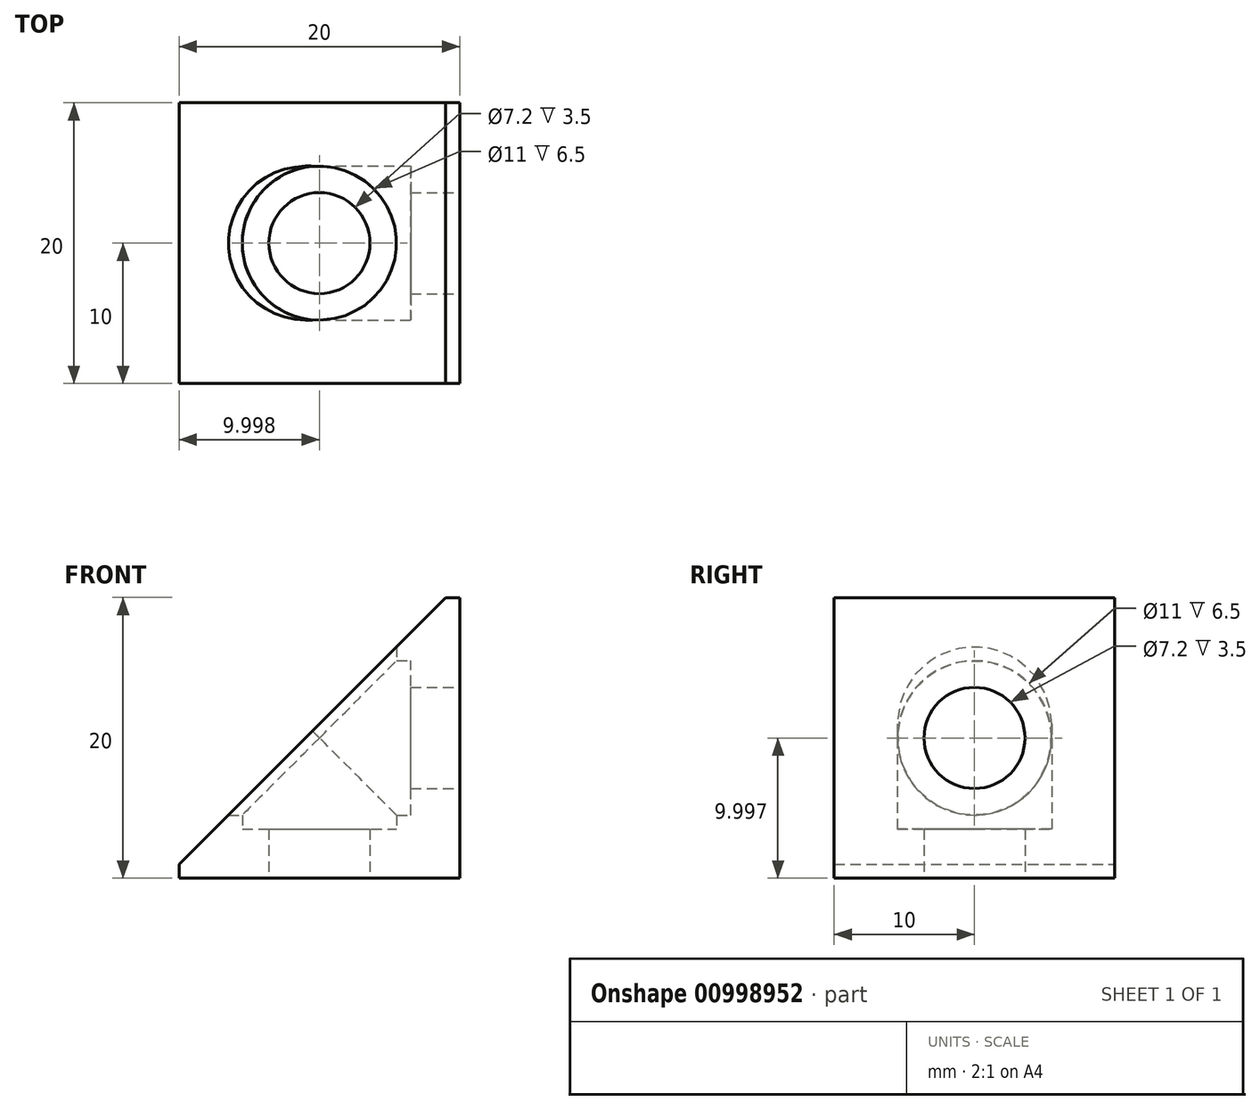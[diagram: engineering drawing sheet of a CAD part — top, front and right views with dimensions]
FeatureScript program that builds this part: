
annotation { "Feature Type Name" : "Feature", "Feature Type Description" : "" }
export const myFeature = defineFeature(function(context is Context, id is Id, definition is map)
    precondition{}
    {
        {
            var Q0;
            Q0=qCreatedBy(makeId("Front.planeOp"),FACE);
            var sketch = newSketch(context, id + "F0", { "sketchPlane" : qUnion([Q0])});
            skLineSegment(sketch, "E0", {"start": v(-13.22, 2.82) * mm, "end": v(6.78, 2.82) * mm});
            skLineSegment(sketch, "E1", {"start": v(6.78, 2.82) * mm, "end": v(6.78, 22.82) * mm});
            skLineSegment(sketch, "E2", {"start": v(6.78, 22.82) * mm, "end": v(5.78, 22.82) * mm});
            skLineSegment(sketch, "E3", {"start": v(5.78, 22.82) * mm, "end": v(-13.22, 3.82) * mm});
            skLineSegment(sketch, "E4", {"start": v(-13.22, 3.82) * mm, "end": v(-13.22, 2.82) * mm});
            skSolve(sketch);
        }
        {
            var Q0;
            Q0=makeQuery(id+"F0.imprint","IMPRINT",FACE,{"disambiguationData":[TD([[makeQuery(id+"F0.imprint","IMPRINT",EDGE,{"derivedFrom":sQuery(id+"F0.wireOp",EDGE,"E0")}),1.0]])]});
            extrude(context, id + "F1", {"entities" : qUnion([Q0]), "depth" : 20 * mm, "offsetDistance" : 25 * mm});
        }
        {
            var Q0;
            Q0=makeQuery(id+"F1.opExtrude","SWEPT_FACE",FACE,{"disambiguationData":[OSD([sQuery(id+"F0.wireOp",EDGE,"E0")])]});
            var sketch = newSketch(context, id + "F2", { "sketchPlane" : qUnion([Q0])});
            skLineSegment(sketch, "E5", {"start": v(-13.22, 20) * mm, "end": v(6.78, 0) * mm, "construction": true});
            skCircle(sketch, "E6", {"center": v(-3.22, 10) * mm, "radius": 3.6 * mm});
            skCircle(sketch, "E7", {"center": v(-3.22, 10) * mm, "radius": 5.5 * mm});
            skSolve(sketch);
        }
        {
            var Q0;
            Q0=makeQuery(id+"F1.opExtrude","SWEPT_FACE",FACE,{"disambiguationData":[OSD([sQuery(id+"F0.wireOp",EDGE,"E1")])]});
            var sketch = newSketch(context, id + "F3", { "sketchPlane" : qUnion([Q0])});
            skLineSegment(sketch, "E8", {"start": v(-20, 22.82) * mm, "end": v(0, 2.82) * mm, "construction": true});
            skCircle(sketch, "E9", {"center": v(-10, 12.82) * mm, "radius": 3.6 * mm});
            skCircle(sketch, "E10", {"center": v(-10, 12.82) * mm, "radius": 5.5 * mm});
            skSolve(sketch);
        }
        {
            var Q0;
            Q0=makeQuery(id+"F3.imprint","IMPRINT",FACE,{"disambiguationData":[TD([[makeQuery(id+"F3.imprint","IMPRINT",EDGE,{"derivedFrom":sQuery(id+"F3.wireOp",EDGE,"E9")}),1.0]])]});
            extrude(context, id + "F4", {"entities" : qUnion([Q0]), "operationType" : NewBodyOperationType.REMOVE, "endBound" : BoundingType.THROUGH_ALL, "oppositeDirection" : true, "depth" : 25 * mm, "offsetDistance" : 25 * mm});
        }
        {
            var Q0;
            Q0=makeQuery(id+"F2.imprint","IMPRINT",FACE,{"disambiguationData":[TD([[makeQuery(id+"F2.imprint","IMPRINT",EDGE,{"derivedFrom":sQuery(id+"F2.wireOp",EDGE,"E6")}),1.0]])]});
            extrude(context, id + "F5", {"entities" : qUnion([Q0]), "operationType" : NewBodyOperationType.REMOVE, "endBound" : BoundingType.THROUGH_ALL, "oppositeDirection" : true, "depth" : 25 * mm, "offsetDistance" : 25 * mm});
        }
        {
            var Q0;
            Q0=makeQuery(id+"F3.imprint","IMPRINT",FACE,{"disambiguationData":[TD([[makeQuery(id+"F3.imprint","IMPRINT",EDGE,{"derivedFrom":sQuery(id+"F3.wireOp",EDGE,"E9")}),-1.0]])]});
            extrude(context, id + "F6", {"entities" : qUnion([Q0]), "operationType" : NewBodyOperationType.REMOVE, "endBound" : BoundingType.THROUGH_ALL, "oppositeDirection" : true, "depth" : 25 * mm, "offsetDistance" : 25 * mm, "hasSecondDirection" : true, "secondDirectionOppositeDirection" : true, "secondDirectionDepth" : 3.5 * mm});
        }
        {
            var Q0;
            Q0=makeQuery(id+"F2.imprint","IMPRINT",FACE,{"disambiguationData":[TD([[makeQuery(id+"F2.imprint","IMPRINT",EDGE,{"derivedFrom":sQuery(id+"F2.wireOp",EDGE,"E6")}),-1.0]])]});
            extrude(context, id + "F7", {"entities" : qUnion([Q0]), "operationType" : NewBodyOperationType.REMOVE, "endBound" : BoundingType.THROUGH_ALL, "oppositeDirection" : true, "depth" : 25 * mm, "offsetDistance" : 25 * mm, "hasSecondDirection" : true, "secondDirectionOppositeDirection" : true, "secondDirectionDepth" : 3.5 * mm});
        }
    });
